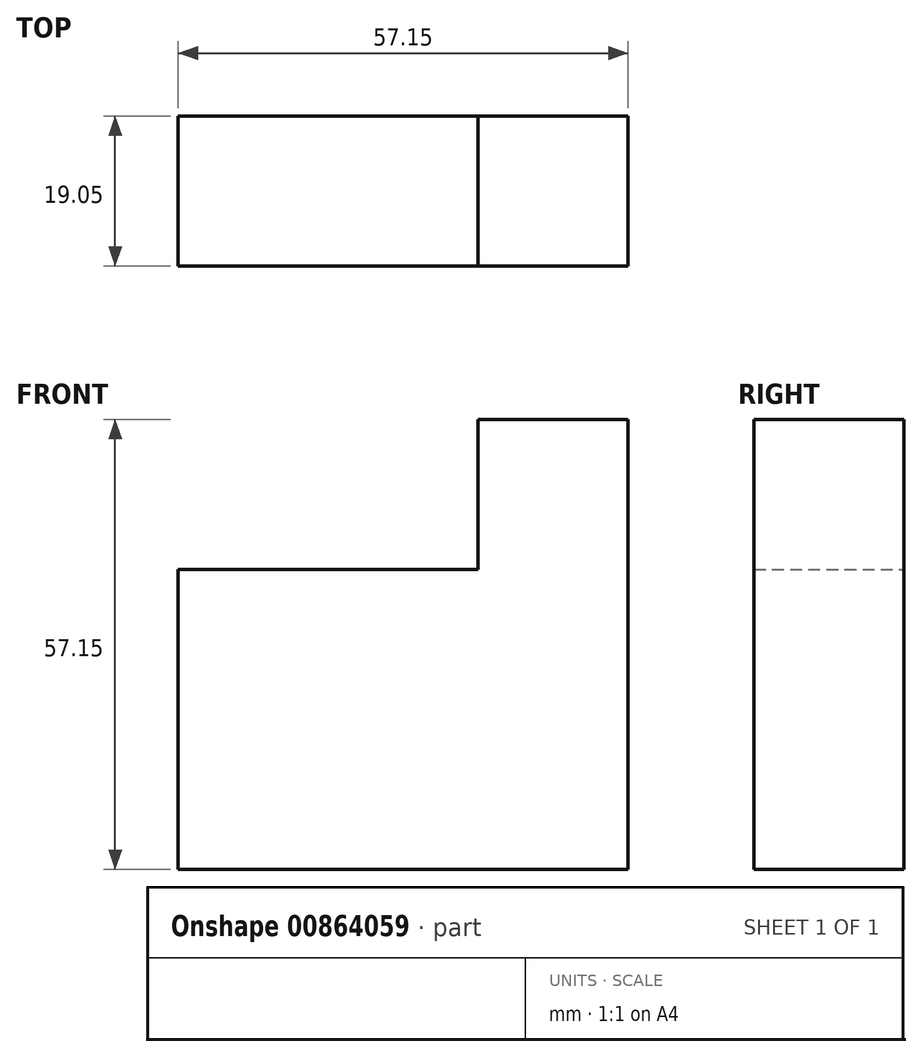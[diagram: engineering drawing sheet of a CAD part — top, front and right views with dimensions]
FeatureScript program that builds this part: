
annotation { "Feature Type Name" : "Feature", "Feature Type Description" : "" }
export const myFeature = defineFeature(function(context is Context, id is Id, definition is map)
    precondition{}
    {
        {
            var Q0;
            Q0=qCreatedBy(makeId("Front.planeOp"),FACE);
            var sketch = newSketch(context, id + "F0", { "sketchPlane" : qUnion([Q0])});
            skLineSegment(sketch, "E0", {"start": v(0, 0) * mm, "end": v(57.15, 0) * mm});
            skLineSegment(sketch, "E1", {"start": v(57.15, 0) * mm, "end": v(57.15, 57.15) * mm});
            skLineSegment(sketch, "E2", {"start": v(57.15, 57.15) * mm, "end": v(38.1, 57.15) * mm});
            skLineSegment(sketch, "E3", {"start": v(38.1, 57.15) * mm, "end": v(38.1, 38.1) * mm});
            skLineSegment(sketch, "E4", {"start": v(38.1, 38.1) * mm, "end": v(0, 38.1) * mm});
            skLineSegment(sketch, "E5", {"start": v(0, 38.1) * mm, "end": v(0, 0) * mm});
            skSolve(sketch);
        }
        {
            var Q0;
            Q0 = qSketchRegion(id + "F0", true);
            extrude(context, id + "F1", {"entities" : qUnion([Q0]), "depth" : 19.05 * mm, "offsetDistance" : 25.4 * mm});
        }
    });
